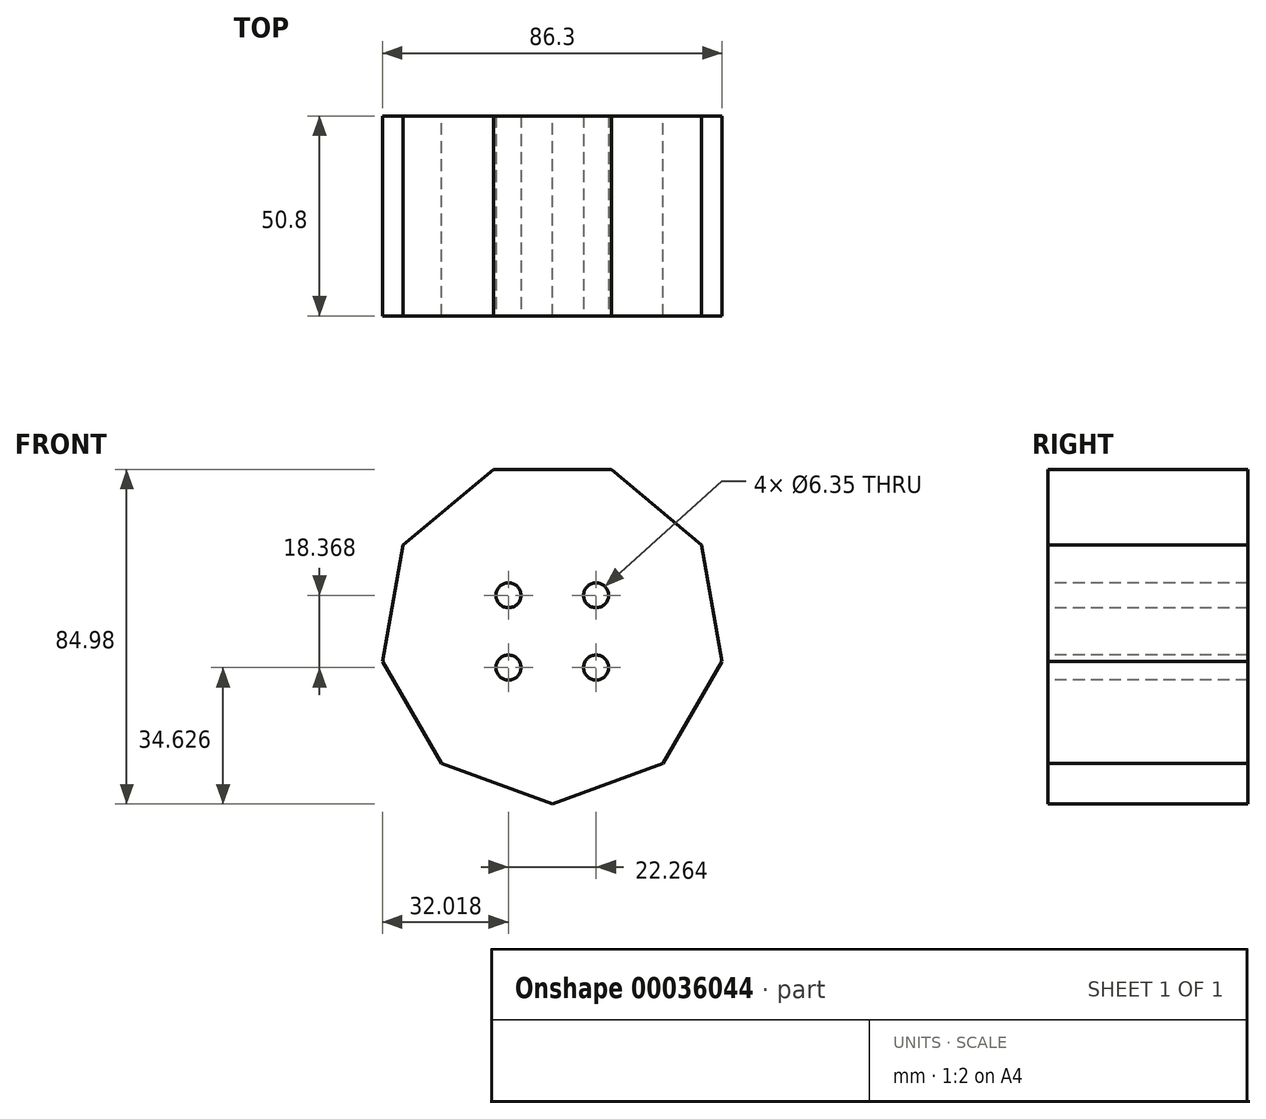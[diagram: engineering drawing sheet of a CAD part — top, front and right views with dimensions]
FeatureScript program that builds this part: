
annotation { "Feature Type Name" : "Feature", "Feature Type Description" : "" }
export const myFeature = defineFeature(function(context is Context, id is Id, definition is map)
    precondition{}
    {
        {
            var Q0;
            Q0=qCreatedBy(makeId("Front.planeOp"),FACE);
            var sketch = newSketch(context, id + "F0", { "sketchPlane" : qUnion([Q0])});
            skCircle(sketch, "E0.cCircle", {"center": v(0, 0) * mm, "radius": 41.17 * mm, "construction": true});
            skLineSegment(sketch, "E0.0", {"start": v(-14.98, 41.17) * mm, "end": v(14.98, 41.17) * mm});
            skLineSegment(sketch, "E0.1", {"start": v(14.98, 41.17) * mm, "end": v(37.94, 21.9) * mm});
            skLineSegment(sketch, "E0.2", {"start": v(37.94, 21.9) * mm, "end": v(43.15, -7.6) * mm});
            skLineSegment(sketch, "E0.3", {"start": v(43.15, -7.6) * mm, "end": v(28.16, -33.56) * mm});
            skLineSegment(sketch, "E0.4", {"start": v(28.16, -33.56) * mm, "end": v(0, -43.81) * mm});
            skLineSegment(sketch, "E0.5", {"start": v(0, -43.81) * mm, "end": v(-28.16, -33.56) * mm});
            skLineSegment(sketch, "E0.6", {"start": v(-28.16, -33.56) * mm, "end": v(-43.15, -7.6) * mm});
            skLineSegment(sketch, "E0.7", {"start": v(-43.15, -7.6) * mm, "end": v(-37.94, 21.9) * mm});
            skLineSegment(sketch, "E0.8", {"start": v(-37.94, 21.9) * mm, "end": v(-14.98, 41.17) * mm});
            skPoint(sketch, "E0.0.midPoint", {"position": v(0, 41.17) * mm});
            skSolve(sketch);
        }
        {
            var Q0;
            Q0 = qSketchRegion(id + "F0", true);
            extrude(context, id + "F1", {"entities" : qUnion([Q0]), "depth" : 25.4 * mm, "hasSecondDirection" : true, "secondDirectionOppositeDirection" : true, "secondDirectionDepth" : 25.4 * mm});
        }
        {
            var Q0;
            Q0=makeQuery(id+"F1.opExtrude","CAP_FACE",FACE,{"disambiguationData":[OSD([sQuery(id+"F0.wireOp",EDGE,"E0.0"),sQuery(id+"F0.wireOp",EDGE,"E0.1"),sQuery(id+"F0.wireOp",EDGE,"E0.2"),sQuery(id+"F0.wireOp",EDGE,"E0.3"),sQuery(id+"F0.wireOp",EDGE,"E0.4"),sQuery(id+"F0.wireOp",EDGE,"E0.5"),sQuery(id+"F0.wireOp",EDGE,"E0.6"),sQuery(id+"F0.wireOp",EDGE,"E0.7"),sQuery(id+"F0.wireOp",EDGE,"E0.8")])],"isStart":false});
            var sketch = newSketch(context, id + "F2", { "sketchPlane" : qUnion([Q0])});
            skPoint(sketch, "E1.rect.middle", {"position": v(0, 0) * mm});
            skPoint(sketch, "E1.rect.right.start.orphan", {"position": v(-11.13, 9.18) * mm});
            skPoint(sketch, "E1.rect.top.end.orphan", {"position": v(-11.13, -9.18) * mm});
            skPoint(sketch, "E1.rect.left.end.orphan", {"position": v(11.13, -9.18) * mm});
            skPoint(sketch, "E1.rect.left.start.orphan", {"position": v(11.13, 9.18) * mm});
            skSolve(sketch);
        }
        {
            var Q0;
            Q0=sQuery(id+"F2.wireOp",VERTEX,"E1.rect.top.end.orphan");
            var Q1;
            Q1=sQuery(id+"F2.wireOp",VERTEX,"E1.rect.right.start.orphan");
            var Q2;
            Q2=sQuery(id+"F2.wireOp",VERTEX,"E1.rect.left.start.orphan");
            var Q3;
            Q3=sQuery(id+"F2.wireOp",VERTEX,"E1.rect.left.end.orphan");
            var Q4;
            Q4=makeQuery(id+"F1.opExtrude","SWEPT_BODY",BODY,{"disambiguationData":[OSD([sQuery(id+"F0.wireOp",EDGE,"E0.0"),sQuery(id+"F0.wireOp",EDGE,"E0.1"),sQuery(id+"F0.wireOp",EDGE,"E0.2"),sQuery(id+"F0.wireOp",EDGE,"E0.3"),sQuery(id+"F0.wireOp",EDGE,"E0.4"),sQuery(id+"F0.wireOp",EDGE,"E0.5"),sQuery(id+"F0.wireOp",EDGE,"E0.6"),sQuery(id+"F0.wireOp",EDGE,"E0.7"),sQuery(id+"F0.wireOp",EDGE,"E0.8")])]});
            hole(context, id + "F3", {"style" : HoleStyle.SIMPLE, "holeDiameter" : 6.35 * mm, "endStyle" : HoleEndStyle.THROUGH, "locations" : qUnion([Q0, Q1, Q2, Q3]), "scope" : qUnion([Q4])});
        }
    });
